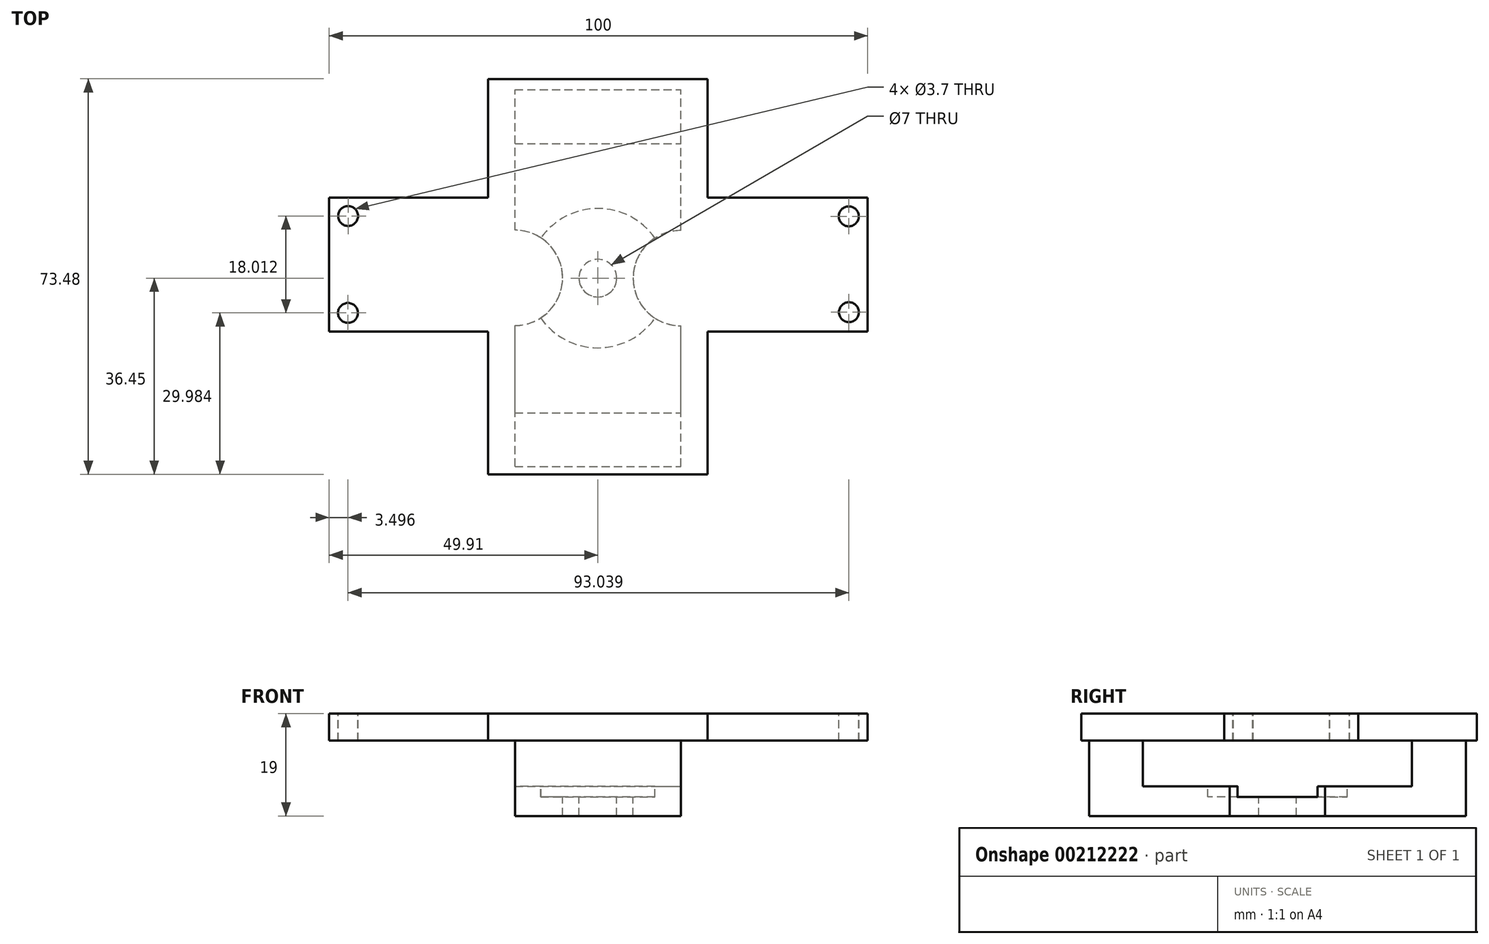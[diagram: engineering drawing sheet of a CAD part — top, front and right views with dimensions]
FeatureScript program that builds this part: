
annotation { "Feature Type Name" : "Feature", "Feature Type Description" : "" }
export const myFeature = defineFeature(function(context is Context, id is Id, definition is map)
    precondition{}
    {
        {
            var Q0;
            Q0=qCreatedBy(makeId("Top.planeOp"),FACE);
            var sketch = newSketch(context, id + "F0", { "sketchPlane" : qUnion([Q0])});
            skLineSegment(sketch, "E0.0", {"start": v(-15.4, 53.06) * mm, "end": v(-15.4, -20.42) * mm});
            skLineSegment(sketch, "E0.1", {"start": v(25.36, 53.06) * mm, "end": v(-15.4, 53.06) * mm});
            skLineSegment(sketch, "E0.2", {"start": v(25.36, -20.42) * mm, "end": v(25.36, 53.06) * mm});
            skLineSegment(sketch, "E0.3", {"start": v(-15.4, -20.42) * mm, "end": v(25.36, -20.42) * mm});
            skSolve(sketch);
        }
        {
            var Q0;
            Q0=makeQuery(id+"F0.imprint","IMPRINT",FACE,{"disambiguationData":[TD([[makeQuery(id+"F0.imprint","IMPRINT",EDGE,{"derivedFrom":sQuery(id+"F0.wireOp",EDGE,"E0.0")}),1.0]])]});
            extrude(context, id + "F1", {"entities" : qUnion([Q0]), "oppositeDirection" : true, "depth" : 5 * mm});
        }
        {
            var Q0;
            Q0=makeQuery(id+"F1.opExtrude","CAP_FACE",FACE,{"disambiguationData":[OSD([sQuery(id+"F0.wireOp",EDGE,"E0.0"),sQuery(id+"F0.wireOp",EDGE,"E0.1"),sQuery(id+"F0.wireOp",EDGE,"E0.2"),sQuery(id+"F0.wireOp",EDGE,"E0.3"),sQuery(id+"F0.wireOp",EDGE,"AwGas1L0-Tx7c-sK6K-lToC-j4NMW9GVDTDE.right")])],"isStart":false});
            var sketch = newSketch(context, id + "F2", { "sketchPlane" : qUnion([Q0])});
            skLineSegment(sketch, "E1.bottom", {"start": v(-10.4, 18.97) * mm, "end": v(20.4, 18.97) * mm});
            skLineSegment(sketch, "E1.top", {"start": v(-10.4, -51.03) * mm, "end": v(20.4, -51.03) * mm});
            skLineSegment(sketch, "E1.left", {"start": v(-10.4, 18.97) * mm, "end": v(-10.4, -7.23) * mm});
            skLineSegment(sketch, "E1.right", {"start": v(20.4, 18.97) * mm, "end": v(20.4, -7.18) * mm});
            skCircle(sketch, "E2", {"center": v(5, -16.03) * mm, "radius": 3.5 * mm});
            skArc(sketch, "E3", {"start": v(20.4, -7.18) * mm, "mid": v(11.55, -16.03) * mm, "end": v(20.4, -24.88) * mm});
            skArc(sketch, "E4", {"start": v(-10.4, -24.93) * mm, "mid": v(-1.55, -16.08) * mm, "end": v(-10.4, -7.23) * mm});
            skLineSegment(sketch, "E5.trimOffspring", {"start": v(-10.4, -16.03) * mm, "end": v(-10.4, -16.08) * mm});
            skLineSegment(sketch, "E6.trimOffspring", {"start": v(-10.4, -24.93) * mm, "end": v(-10.4, -51.03) * mm});
            skLineSegment(sketch, "E7.trimOffspring", {"start": v(20.4, -24.88) * mm, "end": v(20.4, -51.03) * mm});
            skSolve(sketch);
        }
        {
            var Q0;
            Q0=qSketchRegion(id+"F2",true);
            extrude(context, id + "F3", {"entities" : qUnion([Q0]), "operationType" : NewBodyOperationType.ADD, "depth" : 14 * mm});
        }
        {
            var Q0;
            {var subQ0=sQuery(id+"F0.wireOp",EDGE,"AwGas1L0-Tx7c-sK6K-lToC-j4NMW9GVDTDE.right");var subQ1=sQuery(id+"F0.wireOp",EDGE,"E0.0");var subQ2=sQuery(id+"F0.wireOp",EDGE,"E0.1");var subQ3=sQuery(id+"F0.wireOp",EDGE,"E0.2");var subQ4=sQuery(id+"F0.wireOp",EDGE,"E0.3");Q0=makeQuery(id+"F3.boolean.opBoolean","SPLIT",FACE,{"disambiguationData":[TD([makeQuery(id+"F1.opExtrude","SWEPT_FACE",FACE,{"disambiguationData":[OSD([subQ2])]})])],"derivedFrom":makeQuery(id+"F1.opExtrude","CAP_FACE",FACE,{"disambiguationData":[OSD([subQ1,subQ2,subQ3,subQ4,subQ0])],"isStart":false})});}
            var sketch = newSketch(context, id + "F4", { "sketchPlane" : qUnion([Q0])});
            skLineSegment(sketch, "E8.bottom", {"start": v(-14.6, 9.01) * mm, "end": v(20.4, 9.01) * mm});
            skLineSegment(sketch, "E8.top", {"start": v(-14.6, -41) * mm, "end": v(20.4, -41) * mm});
            skLineSegment(sketch, "E8.left", {"start": v(-14.6, 9.01) * mm, "end": v(-14.6, -41) * mm});
            skLineSegment(sketch, "E8.right", {"start": v(20.4, 9.01) * mm, "end": v(20.4, -41) * mm});
            skSolve(sketch);
        }
        {
            var Q0;
            Q0=qSketchRegion(id+"F4",true);
            var Q1;
            Q1=sQuery(id+"F4.wireOp",EDGE,"E8.left");
            extrude(context, id + "F5", {"entities" : qUnion([Q0]), "operationType" : NewBodyOperationType.REMOVE, "surfaceEntities" : qUnion([Q1]), "depth" : 8.5 * mm});
        }
        {
            var Q0;
            {var subQ0=sQuery(id+"F0.wireOp",EDGE,"E0.3");var subQ1=sQuery(id+"F0.wireOp",EDGE,"E0.2");var subQ2=sQuery(id+"F0.wireOp",EDGE,"E0.1");var subQ3=sQuery(id+"F0.wireOp",EDGE,"E0.0");var subQ4=makeQuery(id+"F1.opExtrude","CAP_FACE",FACE,{"disambiguationData":[OSD([subQ3,subQ2,subQ1,subQ0])],"isStart":false});Q0=makeQuery(id+"F5.boolean.opBoolean","MERGE",FACE,{"derivedFrom":[makeQuery(id+"F3.boolean.opBoolean","SPLIT",FACE,{"disambiguationData":[TD([makeQuery(id+"F1.opExtrude","SWEPT_FACE",FACE,{"disambiguationData":[OSD([subQ3])]})])],"derivedFrom":subQ4}),makeQuery(id+"F3.boolean.opBoolean","SPLIT",FACE,{"disambiguationData":[TD([makeQuery(id+"F3.opExtrude","SWEPT_FACE",FACE,{"disambiguationData":[OSD([sQuery(id+"F2.wireOp",EDGE,"wV9iuwiv-zcHe-cE0k-HwwL-fQ0fSy19g1jQ")])]})])],"derivedFrom":subQ4}),makeQuery(id+"F3.boolean.opBoolean","SPLIT",FACE,{"disambiguationData":[TD([makeQuery(id+"F3.opExtrude","SWEPT_FACE",FACE,{"disambiguationData":[OSD([sQuery(id+"F2.wireOp",EDGE,"v6R7sFhp-tAEI-SnQt-5ool-xOl96yPjNEbj")])]})])],"derivedFrom":subQ4}),makeQuery(id+"F5.opExtrude","CAP_FACE",FACE,{"disambiguationData":[OSD([sQuery(id+"F4.wireOp",EDGE,"E8.bottom"),sQuery(id+"F4.wireOp",EDGE,"E8.top"),sQuery(id+"F4.wireOp",EDGE,"E8.left"),sQuery(id+"F4.wireOp",EDGE,"E8.right")])],"isStart":true})]});}
            var sketch = newSketch(context, id + "F6", { "sketchPlane" : qUnion([Q0])});
            skLineSegment(sketch, "E9.bottom", {"start": v(-44.9, -31.01) * mm, "end": v(55.1, -31.01) * mm});
            skLineSegment(sketch, "E9.top", {"start": v(-44.9, -6.1) * mm, "end": v(55.1, -6.1) * mm});
            skLineSegment(sketch, "E9.left", {"start": v(-44.9, -31.01) * mm, "end": v(-44.9, -6.1) * mm});
            skLineSegment(sketch, "E9.right", {"start": v(55.1, -31.01) * mm, "end": v(55.1, -6.1) * mm});
            skPoint(sketch, "E10.endSnap0", {"position": v(4.98, -53.06) * mm});
            skSolve(sketch);
        }
        {
            var Q0;
            Q0=qSketchRegion(id+"F6",true);
            extrude(context, id + "F7", {"entities" : qUnion([Q0]), "operationType" : NewBodyOperationType.ADD, "oppositeDirection" : true, "depth" : 5 * mm});
        }
        {
            var Q0;
            Q0=makeQuery(id+"F7.boolean.opBoolean","MERGE",FACE,{"derivedFrom":[makeQuery(id+"F1.opExtrude","CAP_FACE",FACE,{"disambiguationData":[OSD([sQuery(id+"F0.wireOp",EDGE,"E0.0"),sQuery(id+"F0.wireOp",EDGE,"E0.1"),sQuery(id+"F0.wireOp",EDGE,"E0.2"),sQuery(id+"F0.wireOp",EDGE,"E0.3")])],"isStart":true}),makeQuery(id+"F7.opExtrude","CAP_FACE",FACE,{"disambiguationData":[OSD([sQuery(id+"F6.wireOp",EDGE,"E9.bottom"),sQuery(id+"F6.wireOp",EDGE,"E9.top"),sQuery(id+"F6.wireOp",EDGE,"E9.left"),sQuery(id+"F6.wireOp",EDGE,"E9.right")])],"isStart":false})]});
            var sketch = newSketch(context, id + "F8", { "sketchPlane" : qUnion([Q0])});
            skCircle(sketch, "E11", {"center": v(-41.39, 27.58) * mm, "radius": 1.85 * mm});
            skCircle(sketch, "E12", {"center": v(51.6, 27.51) * mm, "radius": 1.85 * mm});
            skLineSegment(sketch, "E13", {"start": v(-44.9, 31.01) * mm, "end": v(-41.4, 31.01) * mm});
            skCircle(sketch, "E14", {"center": v(-41.41, 9.56) * mm, "radius": 1.85 * mm});
            skCircle(sketch, "E15", {"center": v(51.62, 9.7) * mm, "radius": 1.85 * mm});
            skSolve(sketch);
        }
        {
            var Q0;
            Q0=qSketchRegion(id+"F8",true);
            extrude(context, id + "F9", {"entities" : qUnion([Q0]), "operationType" : NewBodyOperationType.REMOVE, "oppositeDirection" : true, "depth" : 25.4 * mm});
        }
        {
            var Q0;
            Q0=makeQuery(id+"F5.boolean.opBoolean","COPY",FACE,{"derivedFrom":makeQuery(id+"F5.opExtrude","CAP_FACE",FACE,{"disambiguationData":[OSD([sQuery(id+"F4.wireOp",EDGE,"E8.bottom"),sQuery(id+"F4.wireOp",EDGE,"E8.top"),sQuery(id+"F4.wireOp",EDGE,"E8.left"),sQuery(id+"F4.wireOp",EDGE,"E8.right")])],"isStart":false})});
            var sketch = newSketch(context, id + "F10", { "sketchPlane" : qUnion([Q0])});
            skCircle(sketch, "E16", {"center": v(5, 16.03) * mm, "radius": 12.95 * mm});
            skSolve(sketch);
        }
        {
            var Q0;
            Q0 = qSketchRegion(id + "F10", true);
            extrude(context, id + "F11", {"entities" : qUnion([Q0]), "operationType" : NewBodyOperationType.REMOVE, "oppositeDirection" : true, "depth" : 2 * mm});
        }
    });
